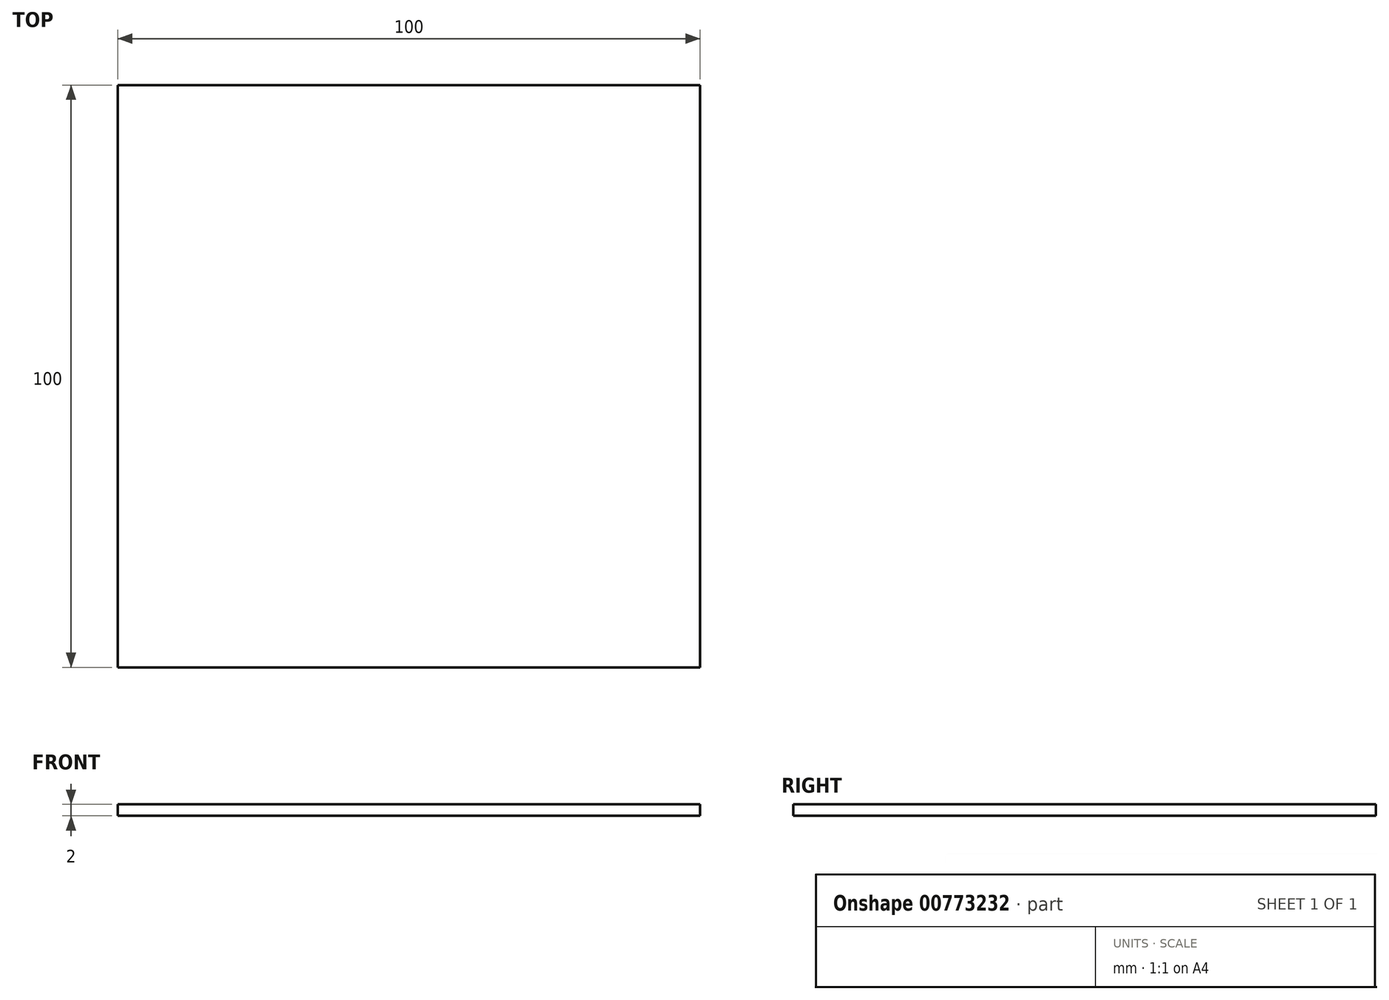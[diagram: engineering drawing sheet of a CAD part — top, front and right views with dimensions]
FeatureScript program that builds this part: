
annotation { "Feature Type Name" : "Feature", "Feature Type Description" : "" }
export const myFeature = defineFeature(function(context is Context, id is Id, definition is map)
    precondition{}
    {
        {
            var Q0;
            Q0=qCreatedBy(makeId("Top.planeOp"),FACE);
            var sketch = newSketch(context, id + "F0", { "sketchPlane" : qUnion([Q0])});
            skLineSegment(sketch, "E0.bottom", {"start": v(-50, 50) * mm, "end": v(50, 50) * mm});
            skLineSegment(sketch, "E0.top", {"start": v(-50, -50) * mm, "end": v(50, -50) * mm});
            skLineSegment(sketch, "E0.left", {"start": v(-50, 50) * mm, "end": v(-50, -50) * mm});
            skLineSegment(sketch, "E0.right", {"start": v(50, 50) * mm, "end": v(50, -50) * mm});
            skSolve(sketch);
        }
        {
            var Q0;
            Q0=makeQuery(id+"F0.imprint","IMPRINT",FACE,{"disambiguationData":[TD([[makeQuery(id+"F0.imprint","IMPRINT",EDGE,{"derivedFrom":sQuery(id+"F0.wireOp",EDGE,"E0.bottom")}),-1.0]])]});
            extrude(context, id + "F1", {"entities" : qUnion([Q0]), "depth" : 2 * mm, "offsetDistance" : 25 * mm});
        }
    });
